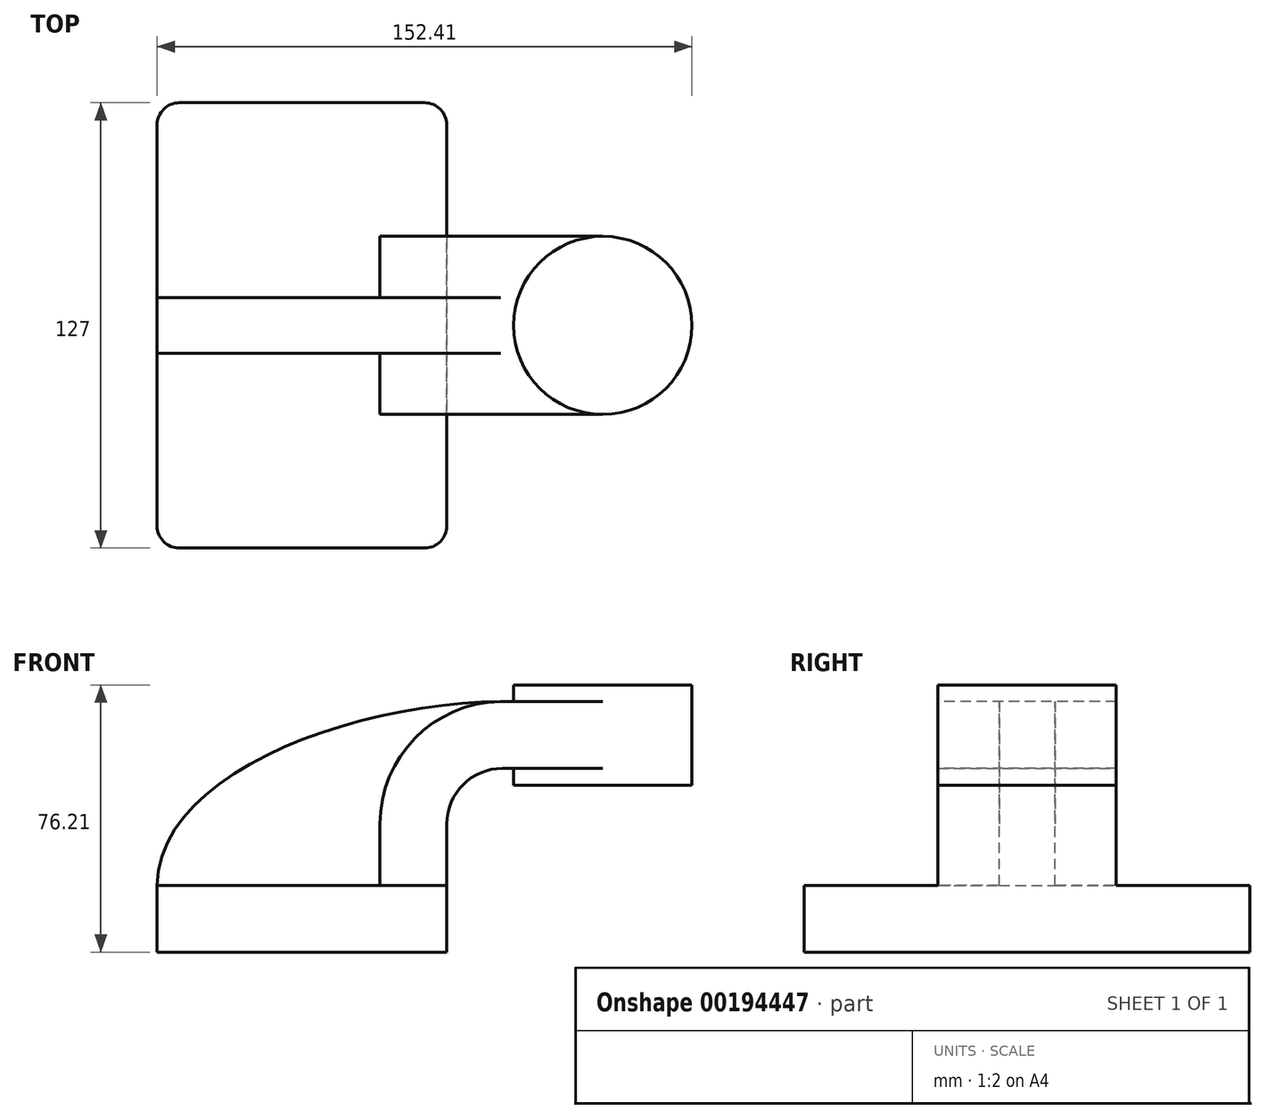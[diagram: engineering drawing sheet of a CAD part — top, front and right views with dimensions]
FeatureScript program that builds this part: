
annotation { "Feature Type Name" : "Feature", "Feature Type Description" : "" }
export const myFeature = defineFeature(function(context is Context, id is Id, definition is map)
    precondition{}
    {
        {
            var Q0;
            Q0=qCreatedBy(makeId("Front.planeOp"),FACE);
            var sketch = newSketch(context, id + "F0", { "sketchPlane" : qUnion([Q0])});
            skLineSegment(sketch, "E0.bottom", {"start": v(41.28, -9.52) * mm, "end": v(-41.27, -9.53) * mm});
            skLineSegment(sketch, "E0.top", {"start": v(41.27, 9.53) * mm, "end": v(-41.28, 9.53) * mm});
            skLineSegment(sketch, "E0.left", {"start": v(41.28, -9.53) * mm, "end": v(41.28, 9.53) * mm});
            skLineSegment(sketch, "E0.right", {"start": v(-41.27, -9.53) * mm, "end": v(-41.28, 9.53) * mm});
            skPoint(sketch, "E0.middle", {"position": v(0, 0) * mm});
            skLineSegment(sketch, "E1.bottom", {"start": v(111.12, 38.1) * mm, "end": v(60.32, 38.1) * mm});
            skLineSegment(sketch, "E1.top", {"start": v(111.12, 66.68) * mm, "end": v(60.32, 66.68) * mm});
            skLineSegment(sketch, "E1.left", {"start": v(111.12, 38.1) * mm, "end": v(111.12, 66.68) * mm});
            skLineSegment(sketch, "E1.right", {"start": v(60.32, 38.1) * mm, "end": v(60.32, 66.68) * mm});
            skPoint(sketch, "E1.middle", {"position": v(85.72, 52.39) * mm});
            skLineSegment(sketch, "E2", {"start": v(41.27, 9.53) * mm, "end": v(41.27, 27) * mm});
            skArc(sketch, "E3", {"start": v(41.27, 27) * mm, "mid": v(45.92, 38.23) * mm, "end": v(57.15, 42.88) * mm});
            skLineSegment(sketch, "E4", {"start": v(57.15, 42.88) * mm, "end": v(85.72, 42.88) * mm});
            skLineSegment(sketch, "E5.0", {"start": v(57.15, 61.93) * mm, "end": v(85.72, 61.93) * mm});
            skArc(sketch, "E5.1", {"start": v(22.23, 27) * mm, "mid": v(32.45, 51.7) * mm, "end": v(57.15, 61.93) * mm});
            skLineSegment(sketch, "E5.2", {"start": v(22.22, 9.53) * mm, "end": v(22.22, 27) * mm});
            skLineSegment(sketch, "E6", {"start": v(85.72, 38.1) * mm, "end": v(85.72, 66.68) * mm});
            skFitSpline(sketch, "E7", {"points": [v(-41.28, 9.52) * mm, v(57.15, 61.93) * mm], "startDerivative": vector(1.36, 98.1) * mm, "endDerivative": vector(123.85, 0.72) * mm});
            skLineSegment(sketch, "E8", {"start": v(85.72, 66.68) * mm, "end": v(85.72, 38.1) * mm});
            skSolve(sketch);
        }
        {
            var Q0;
            Q0=makeQuery(id+"F0.imprint","IMPRINT",FACE,{"disambiguationData":[TD([[makeQuery(id+"F0.imprint","IMPRINT",EDGE,{"derivedFrom":sQuery(id+"F0.wireOp",EDGE,"E0.bottom")}),-1.0]])]});
            extrude(context, id + "F1", {"entities" : qUnion([Q0]), "endBound" : BoundingType.SYMMETRIC, "oppositeDirection" : true, "depth" : 127 * mm});
        }
        {
            var Q0;
            {var subQ1=sQuery(id+"F0.wireOp",EDGE,"E2");Q0=makeQuery(id+"F0.imprint","IMPRINT",FACE,{"disambiguationData":[TD([[makeQuery(id+"F0.imprint","IMPRINT",EDGE,{"derivedFrom":subQ1}),1.0]])]});}
            var Q1;
            {var subQ0=sQuery(id+"F0.wireOp",EDGE,"E4");var subQ1=sQuery(id+"F0.wireOp",EDGE,"E1.right");var subQ2=makeQuery(id+"F0.imprint","INTERSECT",VERTEX,{"derivedFrom":[subQ1,subQ0]});Q1=makeQuery(id+"F0.imprint","IMPRINT",FACE,{"disambiguationData":[TD([[makeQuery(id+"F0.imprint","IMPRINT",EDGE,{"disambiguationData":[TD([[subQ2,-1.0]])],"derivedFrom":subQ1}),-1.0]])]});}
            extrude(context, id + "F2", {"entities" : qUnion([Q0, Q1]), "operationType" : NewBodyOperationType.ADD, "endBound" : BoundingType.SYMMETRIC, "depth" : 50.8 * mm});
        }
        {
            var Q0;
            {var subQ3=sQuery(id+"F0.wireOp",EDGE,"E5.2");Q0=makeQuery(id+"F0.imprint","IMPRINT",FACE,{"disambiguationData":[TD([[makeQuery(id+"F0.imprint","IMPRINT",EDGE,{"derivedFrom":subQ3}),1.0]])]});}
            extrude(context, id + "F3", {"entities" : qUnion([Q0]), "operationType" : NewBodyOperationType.ADD, "endBound" : BoundingType.SYMMETRIC, "depth" : 15.88 * mm});
        }
        {
            var Q0;
            {var subQ4=sQuery(id+"F0.wireOp",EDGE,"E1.left");Q0=makeQuery(id+"F0.imprint","IMPRINT",FACE,{"disambiguationData":[TD([[makeQuery(id+"F0.imprint","IMPRINT",EDGE,{"derivedFrom":subQ4}),1.0]])]});}
            var Q1;
            Q1=sQuery(id+"F0.wireOp",EDGE,"E8");
            revolve(context, id + "F4", {"operationType" : NewBodyOperationType.ADD, "entities" : qUnion([Q0]), "axis" : qUnion([Q1]), "revolveType" : RevolveType.FULL});
        }
        {
            var Q0;
            Q0=makeQuery(id+"F1.opExtrude","CAP_EDGE",EDGE,{"disambiguationData":[OSD([sQuery(id+"F0.wireOp",EDGE,"E0.left")])],"isStart":true});
            var Q1;
            Q1=makeQuery(id+"F1.opExtrude","CAP_EDGE",EDGE,{"disambiguationData":[OSD([sQuery(id+"F0.wireOp",EDGE,"E0.left")])],"isStart":false});
            var Q2;
            Q2=makeQuery(id+"F1.opExtrude","CAP_EDGE",EDGE,{"disambiguationData":[OSD([sQuery(id+"F0.wireOp",EDGE,"E0.right")])],"isStart":false});
            var Q3;
            Q3=makeQuery(id+"F1.opExtrude","CAP_EDGE",EDGE,{"disambiguationData":[OSD([sQuery(id+"F0.wireOp",EDGE,"E0.right")])],"isStart":true});
            fillet(context, id + "F5", {"entities" : qUnion([Q0, Q1, Q2, Q3]), "radius" : 6.35 * mm, "tangentPropagation" : true, "allowEdgeOverflow" : false});
        }
    });
